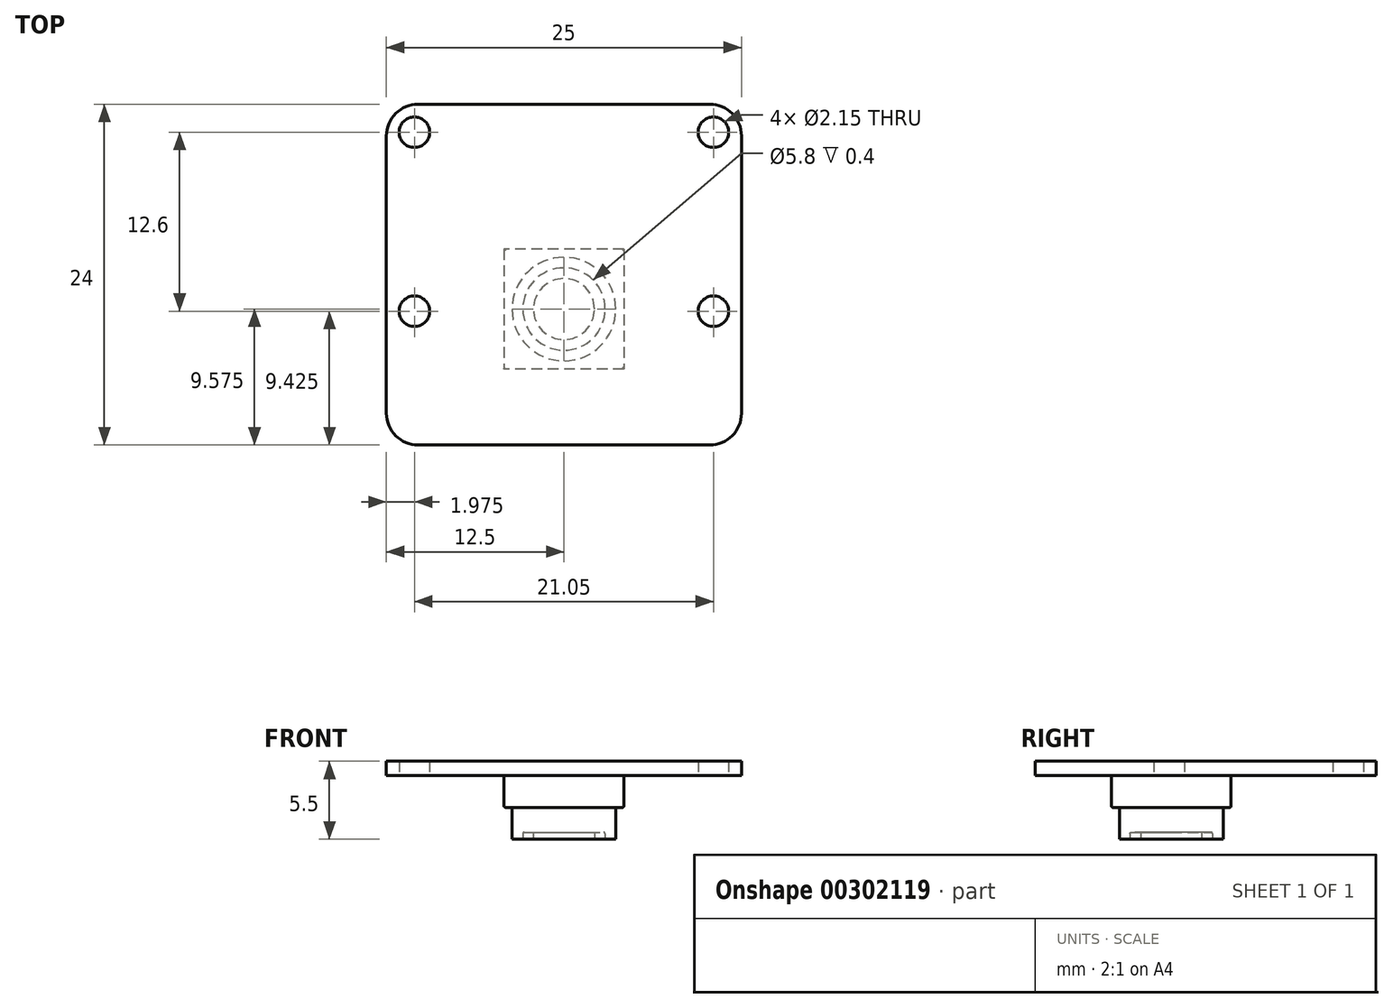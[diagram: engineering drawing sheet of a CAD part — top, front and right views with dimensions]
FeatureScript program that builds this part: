
annotation { "Feature Type Name" : "Feature", "Feature Type Description" : "" }
export const myFeature = defineFeature(function(context is Context, id is Id, definition is map)
    precondition{}
    {
        {
            var Q0;
            Q0=qCreatedBy(makeId("Top.planeOp"),FACE);
            var sketch = newSketch(context, id + "F0", { "sketchPlane" : qUnion([Q0])});
            skLineSegment(sketch, "E0.bottom", {"start": v(10.25, 12) * mm, "end": v(-10.25, 12) * mm});
            skLineSegment(sketch, "E0.top", {"start": v(10.25, -12) * mm, "end": v(-10.25, -12) * mm});
            skLineSegment(sketch, "E0.left", {"start": v(12.5, 9.75) * mm, "end": v(12.5, -9.75) * mm});
            skLineSegment(sketch, "E0.right", {"start": v(-12.5, 9.75) * mm, "end": v(-12.5, -9.75) * mm});
            skPoint(sketch, "E0.middle", {"position": v(0, 0) * mm});
            skCircle(sketch, "E1", {"center": v(-10.53, 10.03) * mm, "radius": 1.07 * mm});
            skCircle(sketch, "E2", {"center": v(10.52, 10.03) * mm, "radius": 1.07 * mm});
            skCircle(sketch, "E3", {"center": v(10.52, -2.57) * mm, "radius": 1.07 * mm});
            skCircle(sketch, "E4", {"center": v(-10.53, -2.57) * mm, "radius": 1.07 * mm});
            skPoint(sketch, "E5.visualSharp", {"position": v(-12.5, -12) * mm});
            skArc(sketch, "E5.filletArc", {"start": v(-12.5, -9.75) * mm, "mid": v(-11.84, -11.34) * mm, "end": v(-10.25, -12) * mm});
            skPoint(sketch, "E6.visualSharp", {"position": v(12.5, -12) * mm});
            skArc(sketch, "E6.filletArc", {"start": v(10.25, -12) * mm, "mid": v(11.84, -11.34) * mm, "end": v(12.5, -9.75) * mm});
            skPoint(sketch, "E7.visualSharp", {"position": v(12.5, 12) * mm});
            skArc(sketch, "E7.filletArc", {"start": v(12.5, 9.75) * mm, "mid": v(11.84, 11.34) * mm, "end": v(10.25, 12) * mm});
            skPoint(sketch, "E8.visualSharp", {"position": v(-12.5, 12) * mm});
            skArc(sketch, "E8.filletArc", {"start": v(-10.25, 12) * mm, "mid": v(-11.84, 11.34) * mm, "end": v(-12.5, 9.75) * mm});
            skSolve(sketch);
        }
        {
            var Q0;
            Q0=makeQuery(id+"F0.imprint","IMPRINT",FACE,{"disambiguationData":[TD([[makeQuery(id+"F0.imprint","IMPRINT",EDGE,{"derivedFrom":sQuery(id+"F0.wireOp",EDGE,"E0.bottom")}),1.0]])]});
            extrude(context, id + "F1", {"entities" : qUnion([Q0]), "depth" : 1 * mm});
        }
        {
            var Q0;
            Q0=makeQuery(id+"F1.opExtrude","CAP_FACE",FACE,{"disambiguationData":[OSD([sQuery(id+"F0.wireOp",EDGE,"E0.bottom"),sQuery(id+"F0.wireOp",EDGE,"E0.top"),sQuery(id+"F0.wireOp",EDGE,"E0.left"),sQuery(id+"F0.wireOp",EDGE,"E0.right"),sQuery(id+"F0.wireOp",EDGE,"E1"),sQuery(id+"F0.wireOp",EDGE,"E2"),sQuery(id+"F0.wireOp",EDGE,"E3"),sQuery(id+"F0.wireOp",EDGE,"E4")])],"isStart":true});
            var sketch = newSketch(context, id + "F2", { "sketchPlane" : qUnion([Q0])});
            skLineSegment(sketch, "E9.bottom", {"start": v(4.21, -1.8) * mm, "end": v(-4.21, -1.8) * mm});
            skLineSegment(sketch, "E9.top", {"start": v(4.22, 6.64) * mm, "end": v(-4.21, 6.64) * mm});
            skLineSegment(sketch, "E9.left", {"start": v(4.21, -1.8) * mm, "end": v(4.22, 6.64) * mm});
            skLineSegment(sketch, "E9.right", {"start": v(-4.21, -1.8) * mm, "end": v(-4.21, 6.64) * mm});
            skPoint(sketch, "E9.middle", {"position": v(0, 2.42) * mm});
            skSolve(sketch);
        }
        {
            var Q0;
            Q0=makeQuery(id+"F2.imprint","IMPRINT",FACE,{"disambiguationData":[TD([[makeQuery(id+"F2.imprint","IMPRINT",EDGE,{"derivedFrom":sQuery(id+"F2.wireOp",EDGE,"E9.bottom")}),-1.0]])]});
            extrude(context, id + "F3", {"entities" : qUnion([Q0]), "operationType" : NewBodyOperationType.ADD, "depth" : 2.25 * mm});
        }
        {
            var Q0;
            Q0=makeQuery(id+"F3.opExtrude","CAP_FACE",FACE,{"disambiguationData":[OSD([sQuery(id+"F2.wireOp",EDGE,"E9.bottom"),sQuery(id+"F2.wireOp",EDGE,"E9.top"),sQuery(id+"F2.wireOp",EDGE,"E9.left"),sQuery(id+"F2.wireOp",EDGE,"E9.right")])],"isStart":false});
            var sketch = newSketch(context, id + "F4", { "sketchPlane" : qUnion([Q0])});
            skCircle(sketch, "E10", {"center": v(0, 2.42) * mm, "radius": 3.65 * mm});
            skLineSegment(sketch, "E11", {"start": v(0, -1.8) * mm, "end": v(0, 6.64) * mm, "construction": true});
            skLineSegment(sketch, "E12", {"start": v(4.22, 2.42) * mm, "end": v(-4.21, 2.42) * mm, "construction": true});
            skSolve(sketch);
        }
        {
            var Q0;
            Q0=makeQuery(id+"F4.imprint","IMPRINT",FACE,{"disambiguationData":[TD([[makeQuery(id+"F4.imprint","IMPRINT",EDGE,{"derivedFrom":sQuery(id+"F4.wireOp",EDGE,"E10")}),1.0]])]});
            extrude(context, id + "F5", {"entities" : qUnion([Q0]), "operationType" : NewBodyOperationType.ADD, "depth" : 2.25 * mm});
        }
        {
            var Q0;
            Q0=makeQuery(id+"F1.opExtrude","CAP_FACE",FACE,{"disambiguationData":[OSD([sQuery(id+"F0.wireOp",EDGE,"E0.bottom"),sQuery(id+"F0.wireOp",EDGE,"E0.top"),sQuery(id+"F0.wireOp",EDGE,"E0.left"),sQuery(id+"F0.wireOp",EDGE,"E0.right"),sQuery(id+"F0.wireOp",EDGE,"E1"),sQuery(id+"F0.wireOp",EDGE,"E2"),sQuery(id+"F0.wireOp",EDGE,"E3"),sQuery(id+"F0.wireOp",EDGE,"E4")])],"isStart":false});
            var sketch = newSketch(context, id + "F6", { "sketchPlane" : qUnion([Q0])});
            skPoint(sketch, "E13", {"position": v(0, -11.7) * mm});
            skSolve(sketch);
        }
        {
            var Q0;
            Q0=makeQuery(id+"F5.opExtrude","CAP_FACE",FACE,{"disambiguationData":[OSD([sQuery(id+"F4.wireOp",EDGE,"E10")])],"isStart":false});
            var sketch = newSketch(context, id + "F7", { "sketchPlane" : qUnion([Q0])});
            skCircle(sketch, "E14", {"center": v(0, 2.42) * mm, "radius": 2.9 * mm});
            skCircle(sketch, "E15", {"center": v(0, 2.42) * mm, "radius": 2.15 * mm});
            skSolve(sketch);
        }
        {
            var Q0;
            Q0=makeQuery(id+"F7.imprint","IMPRINT",FACE,{"disambiguationData":[TD([[makeQuery(id+"F7.imprint","IMPRINT",EDGE,{"derivedFrom":sQuery(id+"F7.wireOp",EDGE,"E14")}),1.0]])]});
            extrude(context, id + "F8", {"entities" : qUnion([Q0]), "operationType" : NewBodyOperationType.REMOVE, "oppositeDirection" : true, "depth" : 0.5 * mm});
        }
        {
            var Q0;
            Q0=makeQuery(id+"F8.boolean.opBoolean","COPY",EDGE,{"derivedFrom":makeQuery(id+"F8.opExtrude","CAP_EDGE",EDGE,{"disambiguationData":[OSD([sQuery(id+"F7.wireOp",EDGE,"E14")])],"isStart":false})});
            var Q1;
            Q1=makeQuery(id+"F8.boolean.opBoolean","COPY",EDGE,{"derivedFrom":makeQuery(id+"F8.opExtrude","CAP_EDGE",EDGE,{"disambiguationData":[OSD([sQuery(id+"F7.wireOp",EDGE,"E14")])],"isStart":true})});
            var Q2;
            Q2=makeQuery(id+"F3.opExtrude","CAP_EDGE",EDGE,{"disambiguationData":[OSD([sQuery(id+"F2.wireOp",EDGE,"E9.bottom")])],"isStart":false});
            var Q3;
            Q3=makeQuery(id+"F3.opExtrude","CAP_EDGE",EDGE,{"disambiguationData":[OSD([sQuery(id+"F2.wireOp",EDGE,"E9.left")])],"isStart":false});
            var Q4;
            Q4=makeQuery(id+"F3.opExtrude","CAP_EDGE",EDGE,{"disambiguationData":[OSD([sQuery(id+"F2.wireOp",EDGE,"E9.top")])],"isStart":false});
            var Q5;
            Q5=makeQuery(id+"F3.opExtrude","CAP_EDGE",EDGE,{"disambiguationData":[OSD([sQuery(id+"F2.wireOp",EDGE,"E9.right")])],"isStart":false});
            fillet(context, id + "F9", {"entities" : qUnion([Q0, Q1, Q2, Q3, Q4, Q5]), "radius" : 0.1 * mm, "tangentPropagation" : true, "allowEdgeOverflow" : false});
        }
    });
